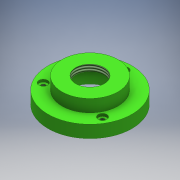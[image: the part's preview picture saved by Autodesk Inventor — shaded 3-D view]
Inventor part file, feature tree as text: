
AUTODESK INVENTOR PART (.ipt)
format: ipt  version: 2016 (Build 200138000, 138)  size: 148,480 bytes
history: native  units: mm
features: sketch x5, extrude x3, hole x2
ambient origin geometry x8: Origin, YZ Plane, XZ Plane, XY Plane, X Axis, Y Axis, Z Axis, Center Point
bodies: Body1 (feature_tree)
feature tree (10):
  extrude  "baseExtrusion"  Depth=10.0mm TaperAngle=0.0deg
  extrude  "objectiveMountExtrusion"  Depth=10.0mm TaperAngle=0.0deg
  hole  "objectiveThread"  [1 undecoded]
  extrude  "objectiveClearance"  Depth=14.7mm
  hole  "holeMounts"  [1 undecoded]
  sketch  "Sketch3"  dims[d7=67.5mm d8=10.0mm d9=0.0mm]
  sketch  "Sketch4"  dims[d10=45.0mm d11=10.0mm d12=0.0mm]
  sketch  "Sketch5"  dims[d13=22.835mm d14=5.3mm d15=4.0mm d16=2.0mm d17=90.0deg d18=59.3mm d19=20.594885mm d20=40.0mm]
  sketch  "Sketch6"  dims[d21=14.7mm d22=0.0mm d23=27.5mm]
  sketch  "Sketch7"  dims[d24=30.0mm d26=360.0deg d28=3.242mm d29=8.0mm d30=7.0mm d31=2.0mm d32=90.0deg d33=11.8mm d34=20.594885mm]
note: 2 required parameter values undecoded (feature->parameter linkage not recoverable at this tier; creation-order binding heuristic only, values carry confidence <= 0.55)
